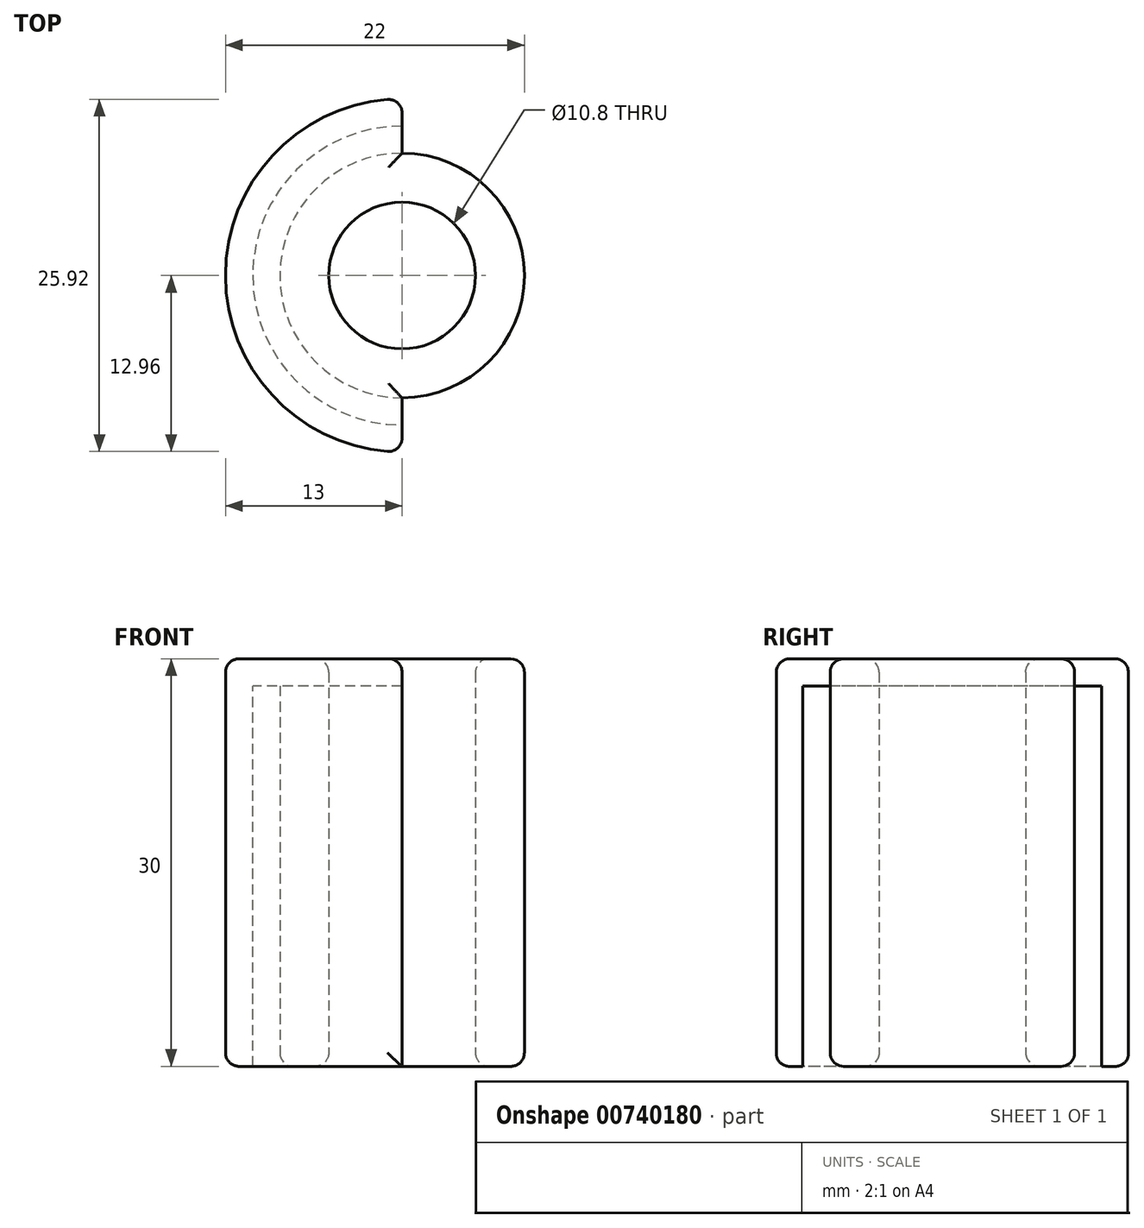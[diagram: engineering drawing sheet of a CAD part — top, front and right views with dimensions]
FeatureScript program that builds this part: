
annotation { "Feature Type Name" : "Feature", "Feature Type Description" : "" }
export const myFeature = defineFeature(function(context is Context, id is Id, definition is map)
    precondition{}
    {
        {
            var Q0;
            Q0=qCreatedBy(makeId("Top.planeOp"),FACE);
            var sketch = newSketch(context, id + "F0", { "sketchPlane" : qUnion([Q0])});
            skCircle(sketch, "E0", {"center": v(0, 0) * mm, "radius": 9 * mm});
            skCircle(sketch, "E1", {"center": v(0, 0) * mm, "radius": 5.4 * mm});
            skSolve(sketch);
        }
        {
            var Q0;
            Q0=makeQuery(id+"F0.imprint","IMPRINT",FACE,{"disambiguationData":[TD([[makeQuery(id+"F0.imprint","IMPRINT",EDGE,{"derivedFrom":sQuery(id+"F0.wireOp",EDGE,"E0")}),1.0]])]});
            extrude(context, id + "F1", {"entities" : qUnion([Q0]), "depth" : 30 * mm, "offsetDistance" : 25 * mm});
        }
        {
            var Q0;
            Q0=makeQuery(id+"F1.opExtrude","CAP_FACE",FACE,{"disambiguationData":[OSD([sQuery(id+"F0.wireOp",EDGE,"E0"),sQuery(id+"F0.wireOp",EDGE,"E1")])],"isStart":false});
            var sketch = newSketch(context, id + "F2", { "sketchPlane" : qUnion([Q0])});
            skArc(sketch, "E2", {"start": v(0, 13) * mm, "mid": v(-13, 0) * mm, "end": v(0, -13) * mm});
            skArc(sketch, "E3", {"start": v(0, 11) * mm, "mid": v(-11, 0) * mm, "end": v(0, -11) * mm});
            skLineSegment(sketch, "E4", {"start": v(0, -13) * mm, "end": v(0, -9) * mm});
            skLineSegment(sketch, "E5", {"start": v(0, 13) * mm, "end": v(0, 9) * mm});
            skSolve(sketch);
        }
        {
            var Q0;
            Q0=makeQuery(id+"F2.imprint","IMPRINT",FACE,{"disambiguationData":[TD([[makeQuery(id+"F2.imprint","IMPRINT",EDGE,{"derivedFrom":sQuery(id+"F2.wireOp",EDGE,"E2")}),1.0]])]});
            var Q1;
            {var subQ3=sQuery(id+"F2.wireOp",EDGE,"E3");Q1=makeQuery(id+"F2.imprint","IMPRINT",FACE,{"disambiguationData":[TD([[makeQuery(id+"F2.imprint","IMPRINT",EDGE,{"derivedFrom":subQ3}),1.0]])]});}
            extrude(context, id + "F3", {"entities" : qUnion([Q0, Q1]), "operationType" : NewBodyOperationType.ADD, "oppositeDirection" : true, "depth" : 2 * mm, "offsetDistance" : 25 * mm});
        }
        {
            var Q0;
            {var subQ0=sQuery(id+"F2.wireOp",EDGE,"E2");Q0=makeQuery(id+"F2.imprint","IMPRINT",FACE,{"disambiguationData":[TD([[makeQuery(id+"F2.imprint","IMPRINT",EDGE,{"derivedFrom":subQ0}),1.0]])]});}
            extrude(context, id + "F4", {"entities" : qUnion([Q0]), "operationType" : NewBodyOperationType.ADD, "oppositeDirection" : true, "depth" : 30 * mm, "offsetDistance" : 25 * mm});
        }
        {
            var Q0;
            Q0=makeQuery(id+"F1.opExtrude","CAP_EDGE",EDGE,{"disambiguationData":[OSD([sQuery(id+"F0.wireOp",EDGE,"E0")])],"isStart":true});
            var Q1;
            Q1=makeQuery(id+"F4.opExtrude","CAP_EDGE",EDGE,{"disambiguationData":[OSD([sQuery(id+"F2.wireOp",EDGE,"E2")])],"isStart":false});
            var Q2;
            Q2=makeQuery(id+"F3.opExtrude","CAP_EDGE",EDGE,{"disambiguationData":[OSD([sQuery(id+"F2.wireOp",EDGE,"E2")])],"isStart":true});
            var Q3;
            {var subQ0=sQuery(id+"F2.wireOp",EDGE,"E5");var subQ1=sQuery(id+"F2.wireOp",EDGE,"E2");Q3=makeQuery(id+"F4.boolean.opBoolean","MERGE",EDGE,{"derivedFrom":[makeQuery(id+"F3.opExtrude","SWEPT_EDGE",EDGE,{"disambiguationData":[OSD([subQ1,subQ0])]}),makeQuery(id+"F4.opExtrude","SWEPT_EDGE",EDGE,{"disambiguationData":[OSD([subQ1,subQ0])]})]});}
            var Q4;
            {var subQ0=sQuery(id+"F2.wireOp",EDGE,"E4");var subQ1=sQuery(id+"F2.wireOp",EDGE,"E2");Q4=makeQuery(id+"F4.boolean.opBoolean","MERGE",EDGE,{"derivedFrom":[makeQuery(id+"F3.opExtrude","SWEPT_EDGE",EDGE,{"disambiguationData":[OSD([subQ1,subQ0])]}),makeQuery(id+"F4.opExtrude","SWEPT_EDGE",EDGE,{"disambiguationData":[OSD([subQ1,subQ0])]})]});}
            var Q5;
            Q5=makeQuery(id+"F3.opExtrude","CAP_EDGE",EDGE,{"disambiguationData":[OSD([sQuery(id+"F2.wireOp",EDGE,"E4")])],"isStart":true});
            var Q6;
            Q6=makeQuery(id+"F3.opExtrude","CAP_EDGE",EDGE,{"disambiguationData":[OSD([sQuery(id+"F2.wireOp",EDGE,"E5")])],"isStart":true});
            var Q7;
            Q7=makeQuery(id+"F1.opExtrude","CAP_EDGE",EDGE,{"disambiguationData":[OSD([sQuery(id+"F0.wireOp",EDGE,"E0")])],"isStart":false});
            var Q8;
            Q8=makeQuery(id+"F1.opExtrude","CAP_EDGE",EDGE,{"disambiguationData":[OSD([sQuery(id+"F0.wireOp",EDGE,"E1")])],"isStart":false});
            var Q9;
            Q9=makeQuery(id+"F1.opExtrude","CAP_EDGE",EDGE,{"disambiguationData":[OSD([sQuery(id+"F0.wireOp",EDGE,"E1")])],"isStart":true});
            fillet(context, id + "F5", {"entities" : qUnion([Q0, Q1, Q2, Q3, Q4, Q5, Q6, Q7, Q8, Q9]), "radius" : 1 * mm, "allowEdgeOverflow" : false});
        }
    });
